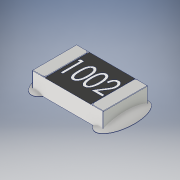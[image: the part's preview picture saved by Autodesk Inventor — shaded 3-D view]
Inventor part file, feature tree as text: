
AUTODESK INVENTOR PART (.ipt)
format: ipt  version: 2019 (Build 230136000, 136)  size: 267,264 bytes
history: native  units: in
note: dims shown in document units (in); Inventor stores cm internally (conversion verified against a paired STEP export)
features: other x2, fillet x1
ambient origin geometry x8: Origin, YZ Plane, XZ Plane, XY Plane, X Axis, Y Axis, Z Axis, Center Point
bodies: Solid1 (feature_tree), Solid2 (feature_tree), Solid3 (feature_tree)
feature tree (3):
  fillet  "Fillet1"  [1 undecoded]
  other  "Body-Move_Copy2"
  other  "Body-Move_Copy4"
note: 1 required parameter value undecoded (feature->parameter linkage not recoverable at this tier; creation-order binding heuristic only, values carry confidence <= 0.55)
